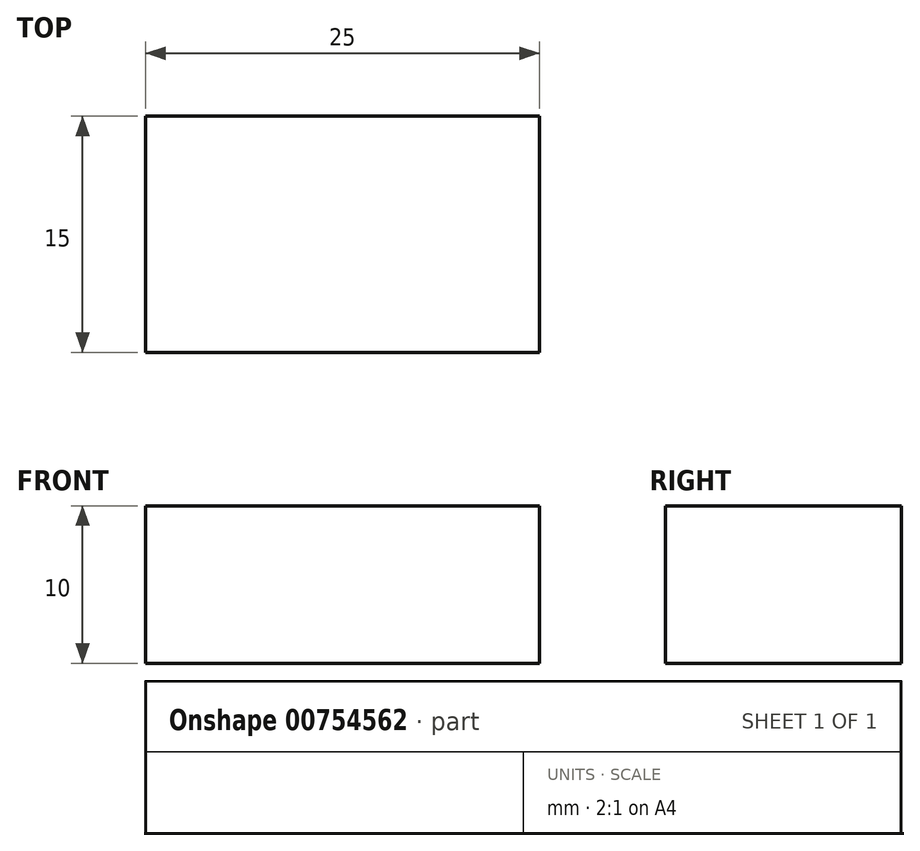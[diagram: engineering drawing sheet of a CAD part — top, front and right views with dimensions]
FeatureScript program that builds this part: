
annotation { "Feature Type Name" : "Feature", "Feature Type Description" : "" }
export const myFeature = defineFeature(function(context is Context, id is Id, definition is map)
    precondition{}
    {
        {
            var Q0;
            Q0=qCreatedBy(makeId("Top.planeOp"),FACE);
            var sketch = newSketch(context, id + "F0", { "sketchPlane" : qUnion([Q0])});
            skLineSegment(sketch, "E0.bottom", {"start": v(12.5, -7.5) * mm, "end": v(-12.5, -7.5) * mm});
            skLineSegment(sketch, "E0.top", {"start": v(12.5, 7.5) * mm, "end": v(-12.5, 7.5) * mm});
            skLineSegment(sketch, "E0.left", {"start": v(12.5, -7.5) * mm, "end": v(12.5, 7.5) * mm});
            skLineSegment(sketch, "E0.right", {"start": v(-12.5, -7.5) * mm, "end": v(-12.5, 7.5) * mm});
            skPoint(sketch, "E0.middle", {"position": v(0, 0) * mm});
            skSolve(sketch);
        }
        {
            var Q0;
            Q0 = qSketchRegion(id + "F0", true);
            extrude(context, id + "F1", {"entities" : qUnion([Q0]), "depth" : 10 * mm, "offsetDistance" : 25 * mm});
        }
    });
